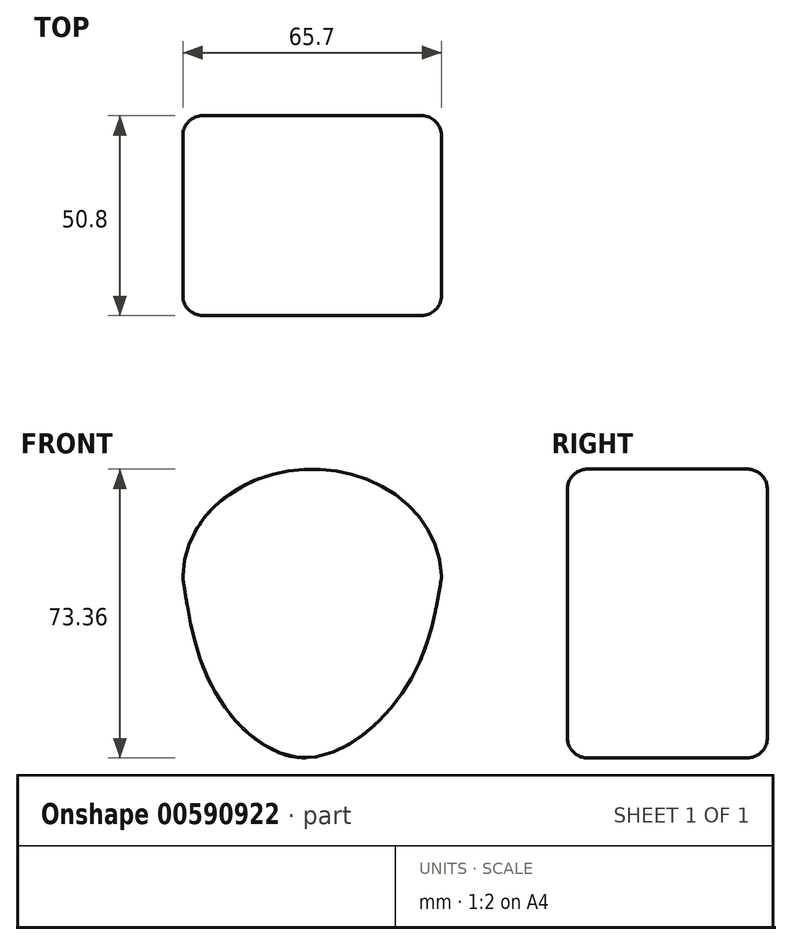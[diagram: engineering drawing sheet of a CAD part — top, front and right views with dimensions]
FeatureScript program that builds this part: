
annotation { "Feature Type Name" : "Feature", "Feature Type Description" : "" }
export const myFeature = defineFeature(function(context is Context, id is Id, definition is map)
    precondition{}
    {
        {
            var Q0;
            Q0=qCreatedBy(makeId("Front.planeOp"),FACE);
            var sketch = newSketch(context, id + "F0", { "sketchPlane" : qUnion([Q0])});
            skEllipse(sketch, "E0", {"center": v(-4.45, 38.44) * mm, "majorRadius": 32.85 * mm, "minorRadius": 27.61 * mm, "majorAxis": v(1, 0)});
            skPoint(sketch, "E1.3.internal.snap0", {"position": v(-4.45, 10.83) * mm});
            skFitSpline(sketch, "E1", {"points": [v(-37.3, 38.44) * mm, v(-28.96, 9.13) * mm, v(-6.21, -7.3) * mm, v(19.56, 10.83) * mm, v(28.4, 38.44) * mm], "startDerivative": vector(18.03, -119.95) * mm, "endDerivative": vector(19.5, 113.68) * mm});
            skSolve(sketch);
        }
        {
            var Q0;
            {var subQ0=sQuery(id+"F0.wireOp",EDGE,"E1");var subQ1=sQuery(id+"F0.wireOp",EDGE,"E0");var subQ2=makeQuery(id+"F0.imprint","INTERSECT",VERTEX,{"disambiguationData":[OD(0.0)],"derivedFrom":[subQ1,subQ0]});Q0=makeQuery(id+"F0.imprint","IMPRINT",FACE,{"disambiguationData":[TD([[makeQuery(id+"F0.imprint","IMPRINT",EDGE,{"disambiguationData":[TD([[subQ2,1.0]])],"derivedFrom":subQ1}),1.0]])]});}
            var Q1;
            {var subQ0=sQuery(id+"F0.wireOp",EDGE,"E1");var subQ1=sQuery(id+"F0.wireOp",EDGE,"E0");var subQ2=makeQuery(id+"F0.imprint","INTERSECT",VERTEX,{"disambiguationData":[OD(2.0)],"derivedFrom":[subQ1,subQ0]});Q1=makeQuery(id+"F0.imprint","IMPRINT",FACE,{"disambiguationData":[TD([[makeQuery(id+"F0.imprint","IMPRINT",EDGE,{"disambiguationData":[TD([[subQ2,-1.0]])],"derivedFrom":subQ1}),-1.0]])]});}
            extrude(context, id + "F1", {"entities" : qUnion([Q0, Q1]), "depth" : 50.8 * mm});
        }
        {
            var Q0;
            Q0=makeQuery(id+"F1.opExtrude","CAP_FACE",FACE,{"disambiguationData":[OSD([sQuery(id+"F0.wireOp",EDGE,"E0"),sQuery(id+"F0.wireOp",EDGE,"E1")])],"isStart":false});
            var sketch = newSketch(context, id + "F2", { "sketchPlane" : qUnion([Q0])});
            skLineSegment(sketch, "E2", {"start": v(-4.45, 66.06) * mm, "end": v(-4.45, -7.2) * mm});
            skLineSegment(sketch, "E3", {"start": v(25.62, 24.91) * mm, "end": v(-34.91, 24.91) * mm});
            skLineSegment(sketch, "E4", {"start": v(-4.45, 10.83) * mm, "end": v(-0.44, 10.83) * mm});
            skLineSegment(sketch, "E5", {"start": v(-0.44, 10.83) * mm, "end": v(-7.4, 10.83) * mm});
            skLineSegment(sketch, "E6", {"start": v(-4.45, 0.56) * mm, "end": v(2.09, 0.56) * mm});
            skLineSegment(sketch, "E7", {"start": v(2.09, 0.56) * mm, "end": v(-10.28, 0.56) * mm});
            skSolve(sketch);
        }
        {
            var Q0;
            Q0=makeQuery(id+"F1.opExtrude","CAP_EDGE",EDGE,{"disambiguationData":[OSD([sQuery(id+"F0.wireOp",EDGE,"E0")])],"isStart":false});
            var Q1;
            Q1=makeQuery(id+"F1.opExtrude","CAP_EDGE",EDGE,{"disambiguationData":[OSD([sQuery(id+"F0.wireOp",EDGE,"E1")])],"isStart":false});
            var Q2;
            Q2=makeQuery(id+"F1.opExtrude","CAP_EDGE",EDGE,{"disambiguationData":[OSD([sQuery(id+"F0.wireOp",EDGE,"E0")])],"isStart":true});
            var Q3;
            Q3=makeQuery(id+"F1.opExtrude","CAP_EDGE",EDGE,{"disambiguationData":[OSD([sQuery(id+"F0.wireOp",EDGE,"E1")])],"isStart":true});
            var Q4;
            Q4=makeQuery(id+"F1.opExtrude","SWEPT_FACE",FACE,{"disambiguationData":[OSD([sQuery(id+"F0.wireOp",EDGE,"E1")])]});
            fillet(context, id + "F3", {"entities" : qUnion([Q0, Q1, Q2, Q3, Q4]), "radius" : 5.08 * mm, "tangentPropagation" : true, "allowEdgeOverflow" : false});
        }
    });
